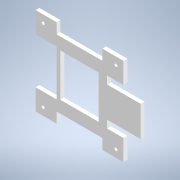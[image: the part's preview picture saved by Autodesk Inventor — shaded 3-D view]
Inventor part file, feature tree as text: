
AUTODESK INVENTOR PART (.ipt)
format: ipt  version: 2020 (Build 240168000, 168)  size: 175,104 bytes
history: native  units: in
note: dims shown in document units (in); Inventor stores cm internally (conversion verified against a paired STEP export)
features: reference x14, other x9, extrude x1, sketch x1
ambient origin geometry x8: Origin, YZ Plane, XZ Plane, XY Plane, X Axis, Y Axis, Z Axis, Center Point
bodies: Body1 (feature_tree)
feature tree (25):
  extrude  "Extrusion3"  Depth=0.5in
  sketch  "Sketch1"  dims[d1=0.5in d2=0.5in d4=0.55in d5=0.55in d6=0.55in d7=0.55in d8=0.55in d9=0.55in d10=0.55in d11=0.55in d20=0.5in d21=0.62in d22=0.1in d23=0.0in]
  reference  "Reference1"
  reference  "Reference2"
  reference  "Reference3"
  reference  "Reference4"
  reference  "Reference5"
  reference  "Reference6"
  reference  "Reference7"
  reference  "Reference8"
  reference  "Reference9"
  reference  "Reference10"
  reference  "Reference11"
  reference  "Reference12"
  reference  "Reference13"
  reference  "Reference14"
  other  "<userpath>\Documents\Inventor\Drone\Assembly.iam"
  other  "Assembly.iam"
  other  "Frame:1"
  other  "F330 Top plate2 v1:1"
  other  "Part5:1"
  other  "VibrationDampener:2"
  other  "VibrationDampener:1"
  other  "DJI F330 qoadrotor arm:3"
  other  "DJI F330 qoadrotor arm v2"
